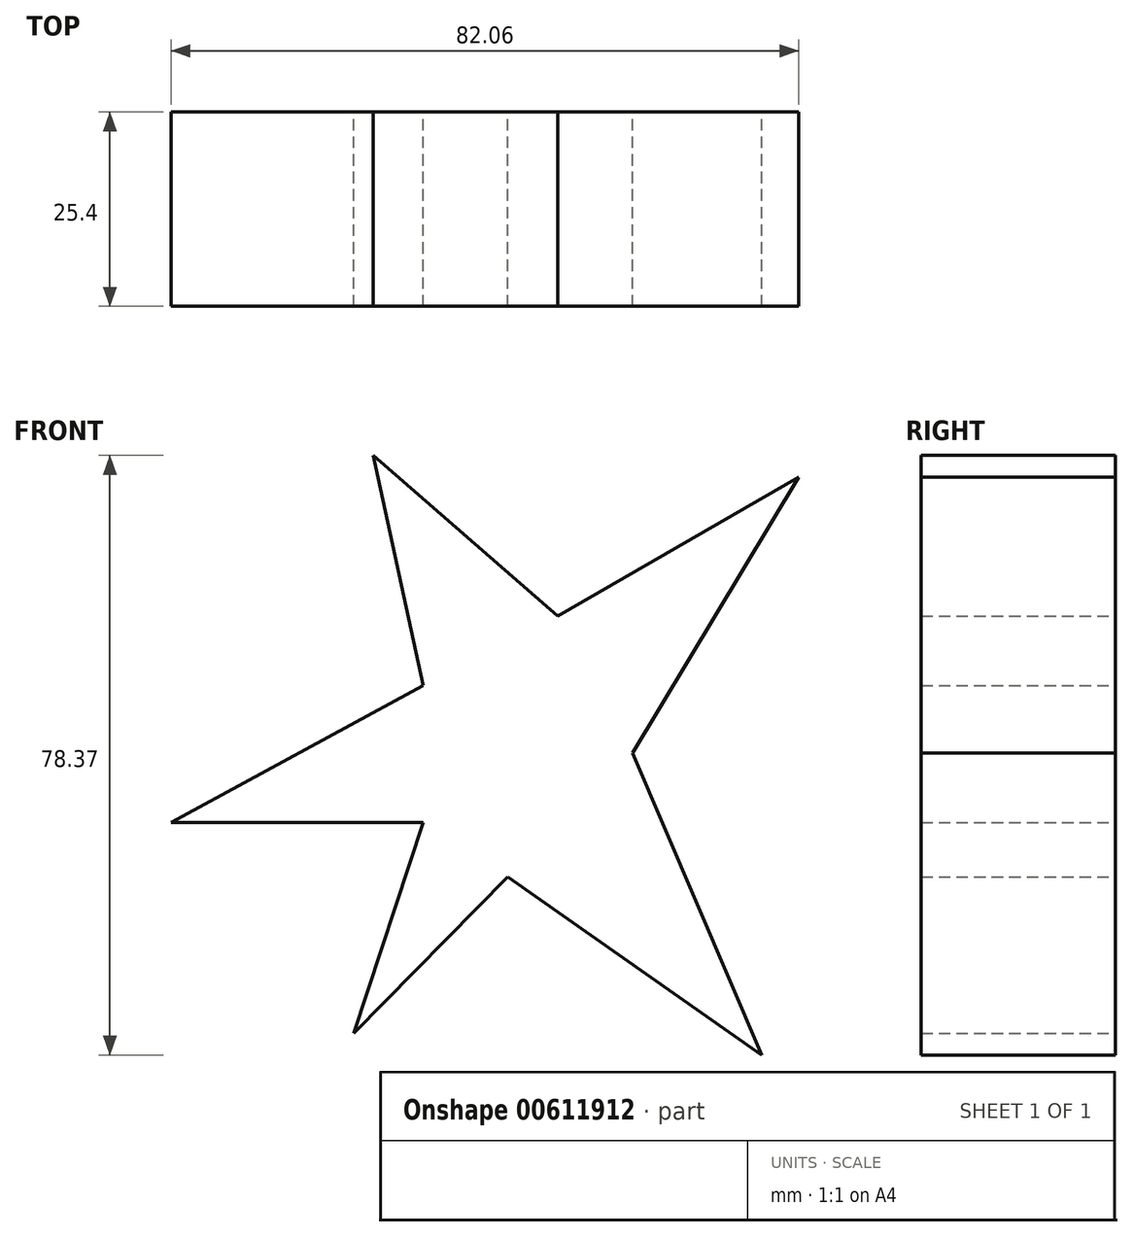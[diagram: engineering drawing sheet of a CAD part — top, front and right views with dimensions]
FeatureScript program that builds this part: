
annotation { "Feature Type Name" : "Feature", "Feature Type Description" : "" }
export const myFeature = defineFeature(function(context is Context, id is Id, definition is map)
    precondition{}
    {
        {
            var Q0;
            Q0=qCreatedBy(makeId("Front.planeOp"),FACE);
            var sketch = newSketch(context, id + "F0", { "sketchPlane" : qUnion([Q0])});
            skLineSegment(sketch, "E0", {"start": v(0, 0) * mm, "end": v(21.72, 36.06) * mm});
            skLineSegment(sketch, "E1", {"start": v(21.72, 36.06) * mm, "end": v(-9.8, 17.89) * mm});
            skLineSegment(sketch, "E2", {"start": v(-9.8, 17.89) * mm, "end": v(-33.93, 38.9) * mm});
            skLineSegment(sketch, "E3", {"start": v(-33.93, 38.9) * mm, "end": v(-27.4, 8.8) * mm});
            skLineSegment(sketch, "E4", {"start": v(-27.4, 8.8) * mm, "end": v(-60.34, -9.09) * mm});
            skLineSegment(sketch, "E5", {"start": v(-60.34, -9.09) * mm, "end": v(-27.4, -9.09) * mm});
            skLineSegment(sketch, "E6", {"start": v(-27.4, -9.09) * mm, "end": v(-36.49, -36.63) * mm});
            skLineSegment(sketch, "E7", {"start": v(-36.49, -36.63) * mm, "end": v(-16.33, -16.18) * mm});
            skLineSegment(sketch, "E8", {"start": v(-16.33, -16.18) * mm, "end": v(16.9, -39.47) * mm});
            skLineSegment(sketch, "E9", {"start": v(16.9, -39.47) * mm, "end": v(0, 0) * mm});
            skSolve(sketch);
        }
        {
            var Q0;
            Q0 = qSketchRegion(id + "F0", true);
            extrude(context, id + "F1", {"entities" : qUnion([Q0]), "depth" : 25.4 * mm, "offsetDistance" : 25.4 * mm});
        }
    });
